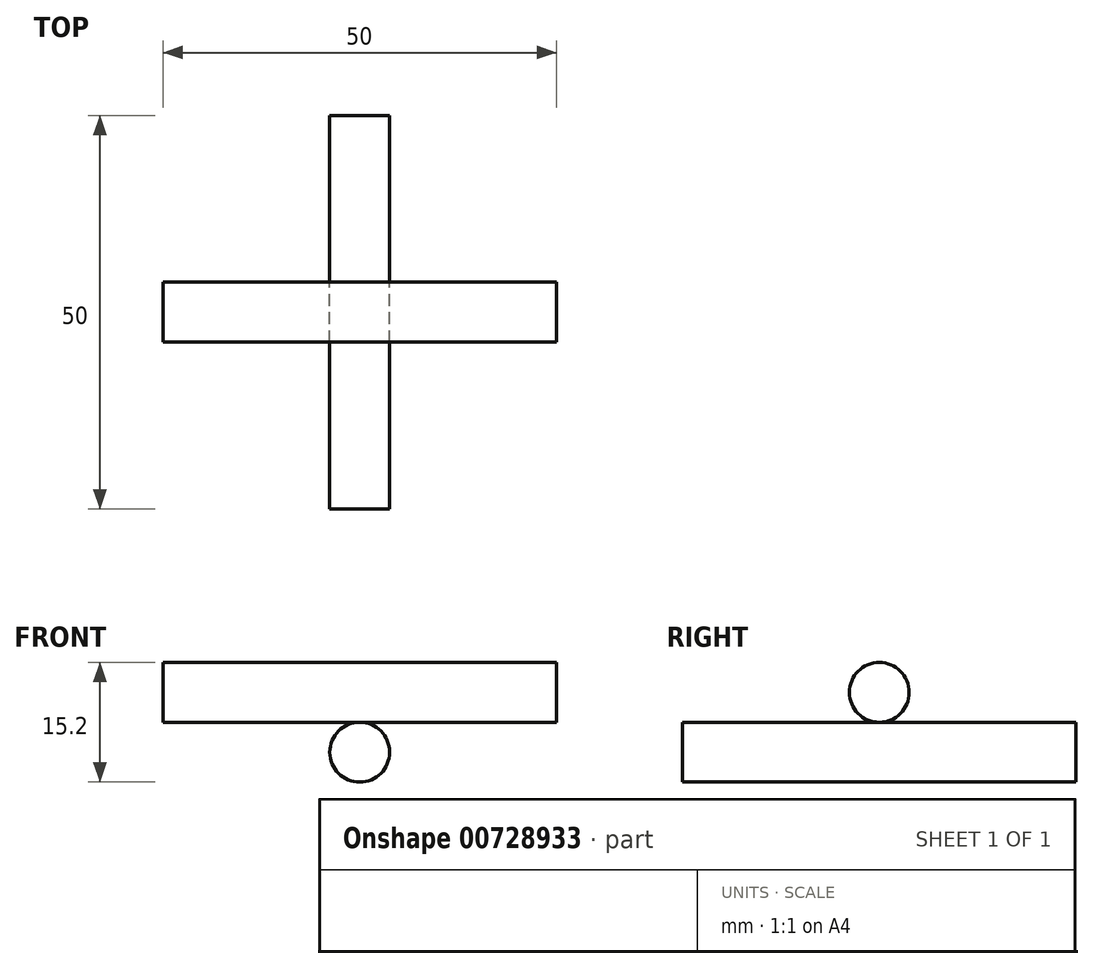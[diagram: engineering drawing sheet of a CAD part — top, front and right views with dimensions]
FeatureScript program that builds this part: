
annotation { "Feature Type Name" : "Feature", "Feature Type Description" : "" }
export const myFeature = defineFeature(function(context is Context, id is Id, definition is map)
    precondition{}
    {
        {
            var Q0;
            Q0=qCreatedBy(makeId("Front.planeOp"),FACE);
            var sketch = newSketch(context, id + "F0", { "sketchPlane" : qUnion([Q0])});
            skCircle(sketch, "E0", {"center": v(0, 0) * mm, "radius": 3.8 * mm});
            skSolve(sketch);
        }
        {
            var Q0;
            Q0=makeQuery(id+"F0.imprint","IMPRINT",FACE,{"disambiguationData":[TD([[makeQuery(id+"F0.imprint","IMPRINT",EDGE,{"derivedFrom":sQuery(id+"F0.wireOp",EDGE,"E0")}),1.0]])]});
            extrude(context, id + "F1", {"entities" : qUnion([Q0]), "endBound" : BoundingType.SYMMETRIC, "depth" : 50 * mm, "offsetDistance" : 25.4 * mm});
        }
        {
            var Q0;
            Q0=qCreatedBy(makeId("Right.planeOp"),FACE);
            var sketch = newSketch(context, id + "F2", { "sketchPlane" : qUnion([Q0])});
            skLineSegment(sketch, "E1", {"start": v(0, 0) * mm, "end": v(0, 7.6) * mm});
            skCircle(sketch, "E2", {"center": v(0, 7.6) * mm, "radius": 3.8 * mm});
            skSolve(sketch);
        }
        {
            var Q0;
            Q0=makeQuery(id+"F2.imprint","IMPRINT",FACE,{"disambiguationData":[TD([[makeQuery(id+"F2.imprint","IMPRINT",EDGE,{"derivedFrom":sQuery(id+"F2.wireOp",EDGE,"E2")}),1.0]])]});
            var Q1;
            Q1=sQuery(id+"F2.wireOp",EDGE,"E2");
            extrude(context, id + "F3", {"entities" : qUnion([Q0]), "surfaceEntities" : qUnion([Q1]), "endBound" : BoundingType.SYMMETRIC, "depth" : 50 * mm, "offsetDistance" : 25.4 * mm});
        }
    });
